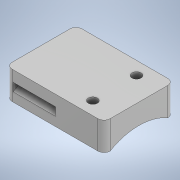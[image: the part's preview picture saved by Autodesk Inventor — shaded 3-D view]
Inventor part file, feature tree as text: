
AUTODESK INVENTOR PART (.ipt)
format: ipt  version: 2021.1 (Build 251245010, 245A)  size: 299,520 bytes
history: native  units: mm
features: move_body x12, other x3, direct_edit x2, fillet x1, extrude x1, sketch x1
ambient origin geometry x8: Origin, YZ Plane, XZ Plane, XY Plane, X Axis, Y Axis, Z Axis, Center Point
bodies: Volumenkörper1 (feature_tree)
feature tree (20):
  direct_edit  "Direktbearbeitung1"
  direct_edit  "Direktbearbeitung2"
  fillet  "Rundung1"  Radius=3.0mm
  extrude  "Extrusion1"  Depth=10.0mm TaperAngle=0.0deg
  sketch  "Skizze1"  dims[d1=3.0mm d2=0.0mm d3=3.0mm d4=0.0mm d5=0.0mm d6=-3.5mm d7=0.0mm d8=0.0mm d9=-0.5mm d10=0.0mm d11=1.75mm d12=0.0mm d13=0.0mm d14=-1.25mm d15=0.0mm d16=0.0mm d17=0.0mm d18=0.0mm d19=-6.75mm d20=0.0mm d21=0.0mm d22=0.5mm d23=0.0mm d24=0.0mm d25=0.5mm d26=0.0mm d27=0.0mm d28=4.5mm d29=0.0mm d30=0.0mm d31=6.5mm d32=2.0mm d33=0.0mm d34=0.0mm d35=1.0mm d36=0.0mm d37=0.0mm d38=1.75mm d39=10.0mm d40=0.0mm]
  other  "Körper1"
  other  "Größe1"
  other  "Größe2"
  move_body  "Verschieben1"
  move_body  "Verschieben2"
  move_body  "Verschieben3"
  move_body  "Verschieben4"
  move_body  "Verschieben5"
  move_body  "Verschieben6"
  move_body  "Verschieben7"
  move_body  "Verschieben8"
  move_body  "Verschieben9"
  move_body  "Verschieben10"
  move_body  "Verschieben11"
  move_body  "Verschieben12"
